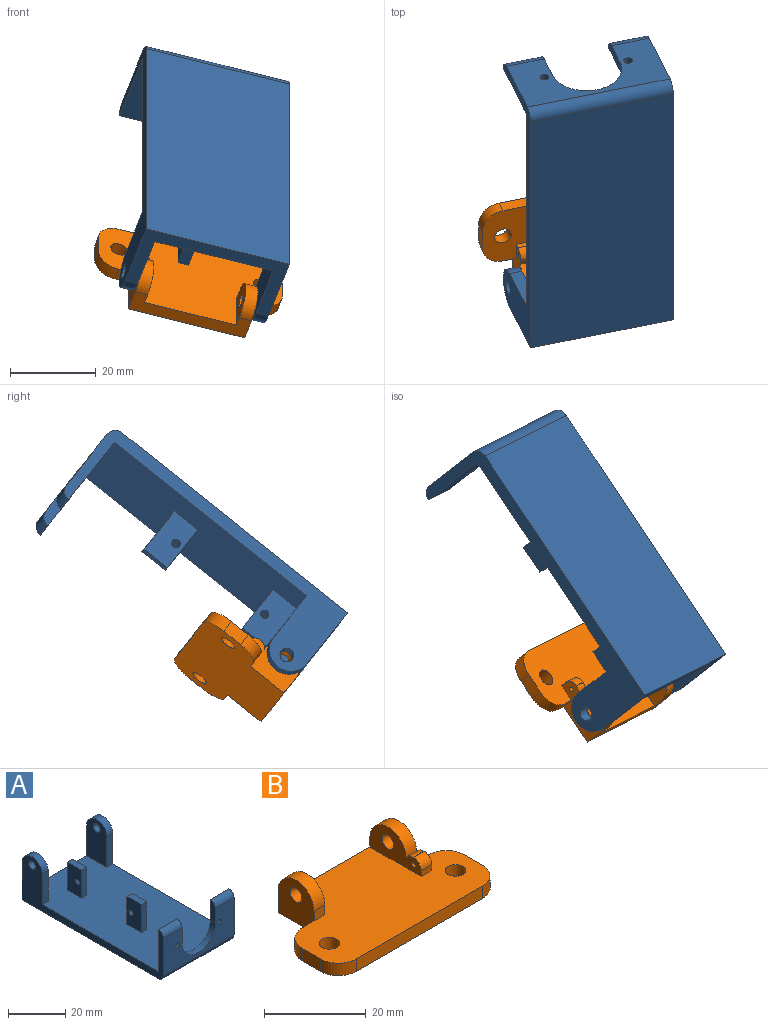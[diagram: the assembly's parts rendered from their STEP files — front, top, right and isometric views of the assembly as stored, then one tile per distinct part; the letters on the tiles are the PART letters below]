
ASSEMBLY  parts=2 mates=1
PART A: 35 faces, bbox 35x70x21 mm
  f0: plane 67.5x35mm, normal (0,0,1), area 2267.5mm2, adj f1,f2,f3,f6,f7,f8,f10,f11
  f1: plane 70x21mm, normal (1,0,0), area 413mm2, adj f0,f4,f5,f15,f24,f25,f26,f28
  f2: plane 12x2.5mm, normal (0,1,0), area 30mm2, adj f0,f6,f7,f9
  f3: plane 70x21mm, normal (-1,0,0), area 413mm2, adj f0,f4,f5,f15,f23,f25,f26,f29
  f4: plane 35x16mm, normal (0,-1,0), area 339.6mm2, adj f1,f3,f16,f17,f18,f19,f20,f23
  f5: plane 67.5x35mm, normal (0,0,-1), area 2362.5mm2, adj f1,f3,f25,f26
  f6: plane 12x7mm, normal (1,0,0), area 80.9mm2, adj f0,f2,f8,f9,f22
  f7: plane 12x7mm, normal (-1,0,0), area 80.9mm2, adj f0,f2,f8,f9,f22
  f8: plane 12x2.5mm, normal (0,-1,0), area 30mm2, adj f0,f6,f7,f9
  f9: plane 7x2.5mm, normal (0,0,1), area 17.5mm2, adj f2,f6,f7,f8
  f10: plane 12x2.5mm, normal (0,-1,0), area 30mm2, adj f0,f11,f13,f14
  f11: plane 12x7mm, normal (1,0,0), area 80.9mm2, adj f0,f10,f12,f14,f21
  f12: plane 12x2.5mm, normal (0,1,0), area 30mm2, adj f0,f11,f13,f14
  f13: plane 12x7mm, normal (-1,0,0), area 80.9mm2, adj f0,f10,f12,f14,f21
  f14: plane 7x2.5mm, normal (0,0,1), area 17.5mm2, adj f10,f11,f12,f13
  f15: plane 35x18mm, normal (0,1,0), area 368.3mm2, adj f0,f1,f3,f16,f17,f18,f19,f20
  f16: cylinder r=8.25mm len=16.5mm, axis (0,-1,0), area 64.8mm2, adj f4,f15,f17,f18
  f17: plane 9x2.5mm, normal (-1,0,0), area 21.2mm2, adj f4,f15,f16,f24
  f18: plane 9x2.5mm, normal (1,0,0), area 21.2mm2, adj f4,f15,f16,f23
  f19: cylinder r=1mm len=2.5mm, axis (0,-1,0), area 15.7mm2, adj f4,f15
  f20: cylinder r=1mm len=2.5mm, axis (0,-1,0), area 15.7mm2, adj f4,f15
  f21: cylinder r=1mm len=2.5mm, axis (1,0,0), area 15.7mm2, adj f11,f13
  f22: cylinder r=1mm len=2.5mm, axis (1,0,0), area 15.7mm2, adj f6,f7
  f23: cylinder r=2.5mm len=9.25mm, axis (-1,0,0), area 36.3mm2, adj f3,f4,f15,f18
  f24: cylinder r=2.5mm len=9.25mm, axis (-1,0,0), area 36.3mm2, adj f1,f4,f15,f17
  f25: cylinder r=2.5mm len=35mm, axis (1,0,0), area 137.4mm2, adj f1,f3,f4,f5
  f26: plane 35x16mm, normal (0,1,0), area 183mm2, adj f0,f1,f3,f5,f27,f30,f33,f34
  f27: plane 18x10mm, normal (-1,0,0), area 160.7mm2, adj f0,f26,f28,f32,f33
  f28: plane 13x3mm, normal (0,-1,0), area 39mm2, adj f0,f1,f27,f33
  f29: plane 13x3mm, normal (0,-1,0), area 39mm2, adj f0,f3,f30,f34
  f30: plane 18x10mm, normal (1,0,0), area 160.7mm2, adj f0,f26,f29,f31,f34
  f31: cylinder r=1.65mm len=3.3mm, axis (1,0,0), area 31.1mm2, adj f3,f30
  f32: cylinder r=1.65mm len=3.3mm, axis (1,0,0), area 31.1mm2, adj f1,f27
  f33: cylinder r=5mm len=10mm, axis (-1,0,0), area 47.1mm2, adj f1,f26,f27,f28
  f34: cylinder r=5mm len=10mm, axis (-1,0,0), area 47.1mm2, adj f3,f26,f29,f30
PART B: 28 faces, bbox 45x25x10.3 mm
  f0: plane 45x25mm, normal (0,0,1), area 840.8mm2, adj f2,f3,f4,f6,f7,f8,f13,f14
  f1: plane 10.3x10mm, normal (-1,0,0), area 83.7mm2, adj f3,f5,f6,f10,f12,f15
  f2: plane 14.2x10.3mm, normal (1,0,0), area 96mm2, adj f0,f3,f5,f9,f11,f13,f23,f24
  f3: plane 28.5x5.3mm, normal (0,1,0), area 99.3mm2, adj f0,f1,f2,f5,f7,f8,f11,f12
  f4: plane 35x3mm, normal (0,-1,0), area 105mm2, adj f0,f5,f20,f21
  f5: plane 45x25mm, normal (0,0,-1), area 913.4mm2, adj f1,f2,f3,f4,f13,f14,f15,f16
  f6: plane 3x2.3mm, normal (0,-1,0), area 6.9mm2, adj f0,f1,f7,f12
  f7: plane 10x7.3mm, normal (1,0,0), area 53.7mm2, adj f0,f3,f6,f10,f12
  f8: plane 14.2x7.3mm, normal (-1,0,0), area 66mm2, adj f0,f3,f9,f11,f23,f24,f25,f26
  f9: cylinder r=1.65mm len=3.3mm, axis (1,0,0), area 31.1mm2, adj f2,f8
  f10: cylinder r=1.65mm len=3.3mm, axis (1,0,0), area 31.1mm2, adj f1,f7
  f11: cylinder r=5mm len=10mm, axis (-1,0,0), area 47.1mm2, adj f2,f3,f8,f26
  f12: cylinder r=5mm len=10mm, axis (1,0,0), area 47.1mm2, adj f1,f3,f6,f7
  f13: plane 3.25x3mm, normal (0,1,0), area 9.8mm2, adj f0,f2,f5,f22
  f14: plane 5x3mm, normal (1,0,0), area 15mm2, adj f0,f5,f21,f22
  f15: plane 3.25x3mm, normal (0,1,0), area 9.7mm2, adj f0,f1,f5,f19
  f16: plane 5x3mm, normal (-1,0,0), area 15mm2, adj f0,f5,f19,f20
  f17: cylinder r=2mm len=4mm, axis (0,0,1), area 37.7mm2, adj f0,f5
  f18: cylinder r=2mm len=4mm, axis (0,0,1), area 37.7mm2, adj f0,f5
  f19: cylinder r=5mm len=5mm, axis (0,0,1), area 23.6mm2, adj f0,f5,f15,f16
  f20: cylinder r=5mm len=5mm, axis (0,0,-1), area 23.6mm2, adj f0,f4,f5,f16
  f21: cylinder r=5mm len=5mm, axis (0,0,-1), area 23.6mm2, adj f0,f4,f5,f14
  f22: cylinder r=5mm len=5mm, axis (0,0,-1), area 23.6mm2, adj f0,f5,f13,f14
  f23: plane 3x1.35mm, normal (0,-1,0), area 4.1mm2, adj f0,f2,f8,f27
  f24: plane 3x0.12mm, normal (0,0,1), area 0.4mm2, adj f2,f8,f26,f27
  f25: cylinder r=0.5mm len=3mm, axis (1,0,0), area 9.4mm2, adj f2,f8
  f26: cylinder r=2.15mm len=3mm, axis (-1,0,0), area 7.2mm2, adj f2,f8,f11,f24
  f27: cylinder r=2.15mm len=3mm, axis (-1,0,0), area 10.1mm2, adj f2,f8,f23,f24
PLACE A rot(axis=(-0.99,-0.05,0.15),141.9deg) t=(2.82,38.9,-7.39)mm
PLACE B rot(axis=(-0.14,0.33,-0.93),174.2deg) t=(-3.85,36.26,-39.08)mm
MATE revolute A.f31 <-> B.f9  axis (0.95,0.19,-0.24) through (-16.26,19.14,-38.74)mm
